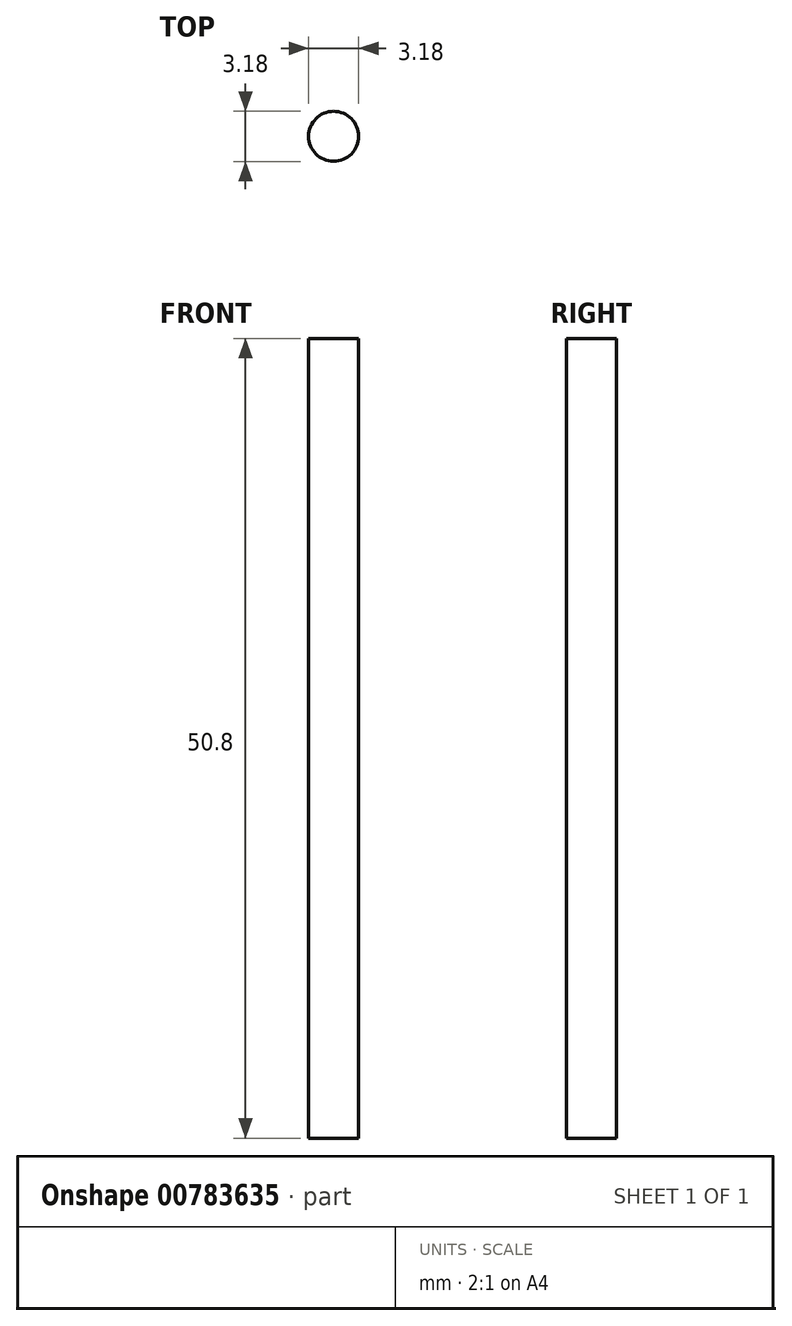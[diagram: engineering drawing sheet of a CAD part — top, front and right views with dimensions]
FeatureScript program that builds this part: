
annotation { "Feature Type Name" : "Feature", "Feature Type Description" : "" }
export const myFeature = defineFeature(function(context is Context, id is Id, definition is map)
    precondition{}
    {
        {
            var Q0;
            Q0=qCreatedBy(makeId("Front.planeOp"),FACE);
            var sketch = newSketch(context, id + "F0", { "sketchPlane" : qUnion([Q0])});
            skLineSegment(sketch, "E0.bottom", {"start": v(-1.59, 36.84) * mm, "end": v(0, 36.84) * mm});
            skLineSegment(sketch, "E0.top", {"start": v(-1.59, -13.96) * mm, "end": v(0, -13.96) * mm});
            skLineSegment(sketch, "E0.left", {"start": v(-1.59, 36.84) * mm, "end": v(-1.59, -13.96) * mm});
            skLineSegment(sketch, "E0.right", {"start": v(0, 36.84) * mm, "end": v(0, -13.96) * mm});
            skSolve(sketch);
        }
        {
            var Q0;
            Q0=makeQuery(id+"F0.imprint","IMPRINT",FACE,{"disambiguationData":[TD([[makeQuery(id+"F0.imprint","IMPRINT",EDGE,{"derivedFrom":sQuery(id+"F0.wireOp",EDGE,"E0.bottom")}),-1.0]])]});
            var Q1;
            Q1=sQuery(id+"F0.wireOp",EDGE,"E0.left");
            var Q2;
            Q2=sQuery(id+"F0.wireOp",EDGE,"E0.right");
            revolve(context, id + "F1", {"surfaceOperationType" : NewSurfaceOperationType.NEW, "entities" : qUnion([Q0]), "surfaceEntities" : qUnion([Q1]), "axis" : qUnion([Q2]), "revolveType" : RevolveType.FULL});
        }
    });
